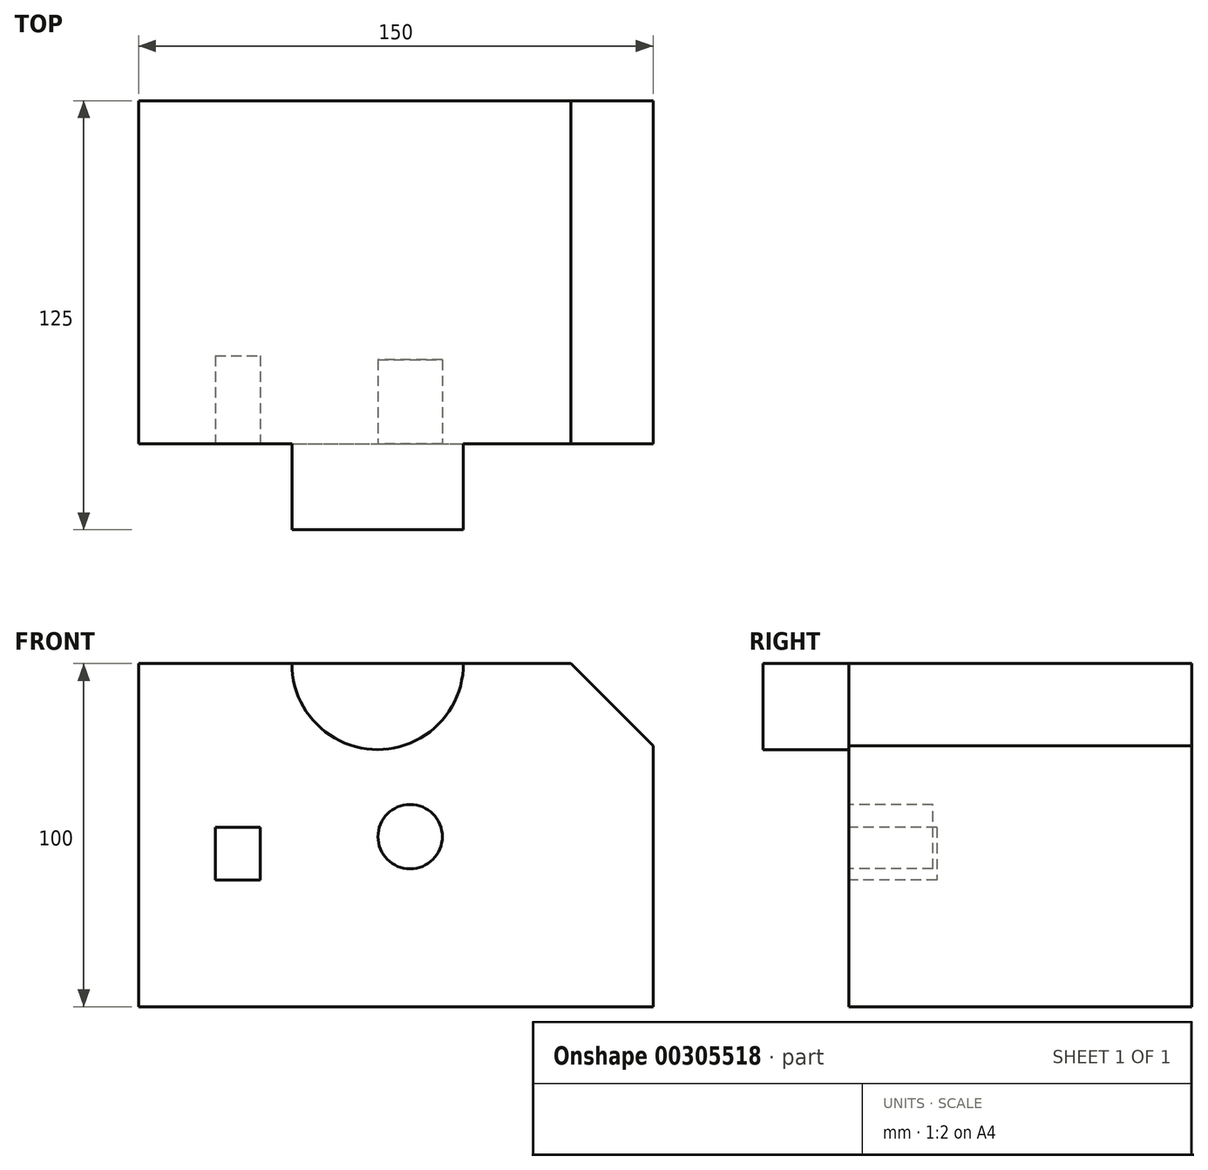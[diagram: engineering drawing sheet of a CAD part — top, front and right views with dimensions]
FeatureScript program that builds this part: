
annotation { "Feature Type Name" : "Feature", "Feature Type Description" : "" }
export const myFeature = defineFeature(function(context is Context, id is Id, definition is map)
    precondition{}
    {
        {
            var Q0;
            Q0=qCreatedBy(makeId("Front.planeOp"),FACE);
            var sketch = newSketch(context, id + "F0", { "sketchPlane" : qUnion([Q0])});
            skLineSegment(sketch, "E0.bottom", {"start": v(-59.62, 58.1) * mm, "end": v(90.38, 58.1) * mm});
            skLineSegment(sketch, "E0.top", {"start": v(-59.62, -41.9) * mm, "end": v(90.38, -41.9) * mm});
            skLineSegment(sketch, "E0.left", {"start": v(-59.62, 58.1) * mm, "end": v(-59.62, -41.9) * mm});
            skLineSegment(sketch, "E0.right", {"start": v(90.38, 58.1) * mm, "end": v(90.38, -41.9) * mm});
            skSolve(sketch);
        }
        {
            var Q0;
            Q0=makeQuery(id+"F0.imprint","IMPRINT",FACE,{"disambiguationData":[TD([[makeQuery(id+"F0.imprint","IMPRINT",EDGE,{"derivedFrom":sQuery(id+"F0.wireOp",EDGE,"E0.bottom")}),-1.0]])]});
            extrude(context, id + "F1", {"entities" : qUnion([Q0]), "depth" : 100 * mm});
        }
        {
            var Q0;
            Q0=makeQuery(id+"F1.opExtrude","CAP_FACE",FACE,{"disambiguationData":[OSD([sQuery(id+"F0.wireOp",EDGE,"E0.bottom"),sQuery(id+"F0.wireOp",EDGE,"E0.top"),sQuery(id+"F0.wireOp",EDGE,"E0.left"),sQuery(id+"F0.wireOp",EDGE,"E0.right")])],"isStart":false});
            var sketch = newSketch(context, id + "F2", { "sketchPlane" : qUnion([Q0])});
            skSolve(sketch);
        }
        {
            var Q0;
            Q0=makeQuery(id+"F2.imprint","IMPRINT",FACE,{"disambiguationData":[TD([[makeQuery(id+"F2.imprint","IMPRINT",EDGE,{"derivedFrom":makeQuery(id+"F1.opExtrude","CAP_EDGE",EDGE,{"disambiguationData":[OSD([sQuery(id+"F0.wireOp",EDGE,"E0.bottom")])],"isStart":false})}),-1.0]])]});
            var sketch = newSketch(context, id + "F3", { "sketchPlane" : qUnion([Q0])});
            skCircle(sketch, "E1", {"center": v(10.06, 58.03) * mm, "radius": 25 * mm});
            skSolve(sketch);
        }
        {
            var Q0;
            {var subQ0=sQuery(id+"F3.wireOp",EDGE,"E1");var subQ1=makeQuery(id+"F2.imprint","IMPRINT",EDGE,{"derivedFrom":makeQuery(id+"F1.opExtrude","CAP_EDGE",EDGE,{"disambiguationData":[OSD([sQuery(id+"F0.wireOp",EDGE,"E0.bottom")])],"isStart":false})});var subQ2=makeQuery(id+"F3.imprint","INTERSECT",VERTEX,{"disambiguationData":[OD(0.0)],"derivedFrom":[subQ1,subQ0]});Q0=makeQuery(id+"F3.imprint","IMPRINT",FACE,{"disambiguationData":[TD([[makeQuery(id+"F3.imprint","IMPRINT",EDGE,{"disambiguationData":[TD([[subQ2,-1.0]])],"derivedFrom":subQ0}),1.0]])]});}
            extrude(context, id + "F4", {"entities" : qUnion([Q0]), "operationType" : NewBodyOperationType.ADD, "depth" : 25 * mm});
        }
        {
            var Q0;
            Q0=makeQuery(id+"F1.opExtrude","SWEPT_EDGE",EDGE,{"disambiguationData":[OSD([sQuery(id+"F0.wireOp",EDGE,"E0.bottom"),sQuery(id+"F0.wireOp",EDGE,"E0.right")])]});
            chamfer(context, id + "F5", {"entities" : qUnion([Q0]), "width" : 24 * mm, "tangentPropagation" : true});
        }
        {
            var Q0;
            Q0=makeQuery(id+"F2.imprint","IMPRINT",FACE,{"disambiguationData":[TD([[makeQuery(id+"F2.imprint","IMPRINT",EDGE,{"derivedFrom":makeQuery(id+"F1.opExtrude","CAP_EDGE",EDGE,{"disambiguationData":[OSD([sQuery(id+"F0.wireOp",EDGE,"E0.bottom")])],"isStart":false})}),-1.0]])]});
            var sketch = newSketch(context, id + "F6", { "sketchPlane" : qUnion([Q0])});
            skCircle(sketch, "E2", {"center": v(19.54, 7.65) * mm, "radius": 9.38 * mm});
            skSolve(sketch);
        }
        {
            var Q0;
            Q0=makeQuery(id+"F6.imprint","IMPRINT",FACE,{"disambiguationData":[TD([[makeQuery(id+"F6.imprint","IMPRINT",EDGE,{"derivedFrom":sQuery(id+"F6.wireOp",EDGE,"E2")}),1.0]])]});
            var Q1;
            Q1=sQuery(id+"F6.wireOp",EDGE,"E2");
            extrude(context, id + "F7", {"entities" : qUnion([Q0]), "operationType" : NewBodyOperationType.REMOVE, "surfaceEntities" : qUnion([Q1]), "oppositeDirection" : true, "depth" : 24.5 * mm});
        }
        {
            var Q0;
            Q0=makeQuery(id+"F2.imprint","IMPRINT",FACE,{"disambiguationData":[TD([[makeQuery(id+"F2.imprint","IMPRINT",EDGE,{"derivedFrom":makeQuery(id+"F1.opExtrude","CAP_EDGE",EDGE,{"disambiguationData":[OSD([sQuery(id+"F0.wireOp",EDGE,"E0.bottom")])],"isStart":false})}),-1.0]])]});
            var sketch = newSketch(context, id + "F8", { "sketchPlane" : qUnion([Q0])});
            skLineSegment(sketch, "E3.bottom", {"start": v(-37.24, 10.37) * mm, "end": v(-24.16, 10.37) * mm});
            skLineSegment(sketch, "E3.top", {"start": v(-37.24, -4.94) * mm, "end": v(-24.16, -4.94) * mm});
            skLineSegment(sketch, "E3.left", {"start": v(-37.24, 10.37) * mm, "end": v(-37.24, -4.94) * mm});
            skLineSegment(sketch, "E3.right", {"start": v(-24.16, 10.37) * mm, "end": v(-24.16, -4.94) * mm});
            skSolve(sketch);
        }
        {
            var Q0;
            Q0 = qSketchRegion(id + "F8", true);
            extrude(context, id + "F9", {"entities" : qUnion([Q0]), "operationType" : NewBodyOperationType.REMOVE, "oppositeDirection" : true, "depth" : 25.7 * mm});
        }
    });
